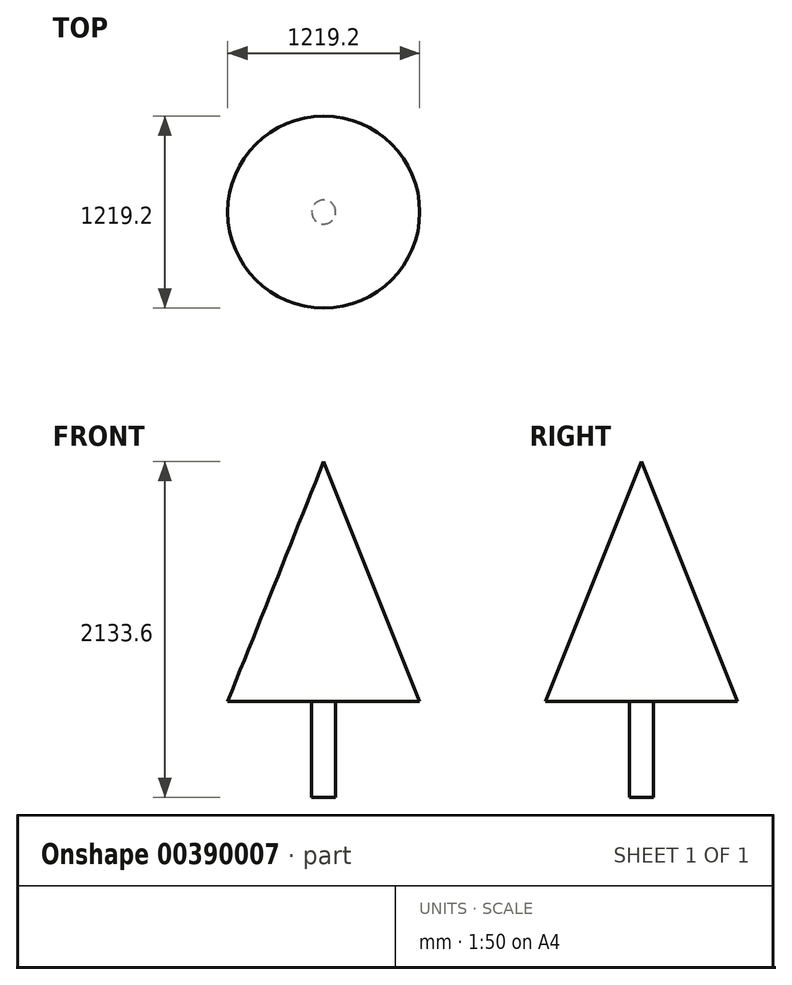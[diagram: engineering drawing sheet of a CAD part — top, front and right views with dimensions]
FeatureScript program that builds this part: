
annotation { "Feature Type Name" : "Feature", "Feature Type Description" : "" }
export const myFeature = defineFeature(function(context is Context, id is Id, definition is map)
    precondition{}
    {
        {
            var Q0;
            Q0=qCreatedBy(makeId("Top.planeOp"),FACE);
            var sketch = newSketch(context, id + "F0", { "sketchPlane" : qUnion([Q0])});
            skCircle(sketch, "E0", {"center": v(0, 0) * mm, "radius": 76.2 * mm});
            skSolve(sketch);
        }
        {
            var Q0;
            Q0=makeQuery(id+"F0.imprint","IMPRINT",FACE,{"disambiguationData":[TD([[makeQuery(id+"F0.imprint","IMPRINT",EDGE,{"derivedFrom":sQuery(id+"F0.wireOp",EDGE,"E0")}),1.0]])]});
            extrude(context, id + "F1", {"entities" : qUnion([Q0]), "depth" : 609.6 * mm});
        }
        {
            var Q0;
            Q0=qCreatedBy(makeId("Front.planeOp"),FACE);
            var sketch = newSketch(context, id + "F2", { "sketchPlane" : qUnion([Q0])});
            skLineSegment(sketch, "E1", {"start": v(0, 609.6) * mm, "end": v(0, 2133.6) * mm});
            skLineSegment(sketch, "E2", {"start": v(0, 609.6) * mm, "end": v(609.6, 609.6) * mm});
            skLineSegment(sketch, "E3", {"start": v(0, 2133.6) * mm, "end": v(609.6, 609.6) * mm});
            skSolve(sketch);
        }
        {
            var Q0;
            Q0=makeQuery(id+"F2.imprint","IMPRINT",FACE,{"disambiguationData":[TD([[makeQuery(id+"F2.imprint","IMPRINT",EDGE,{"derivedFrom":sQuery(id+"F2.wireOp",EDGE,"E1")}),-1.0]])]});
            var Q1;
            Q1=sQuery(id+"F2.wireOp",EDGE,"E1");
            revolve(context, id + "F3", {"operationType" : NewBodyOperationType.ADD, "entities" : qUnion([Q0]), "axis" : qUnion([Q1]), "revolveType" : RevolveType.FULL});
        }
    });
